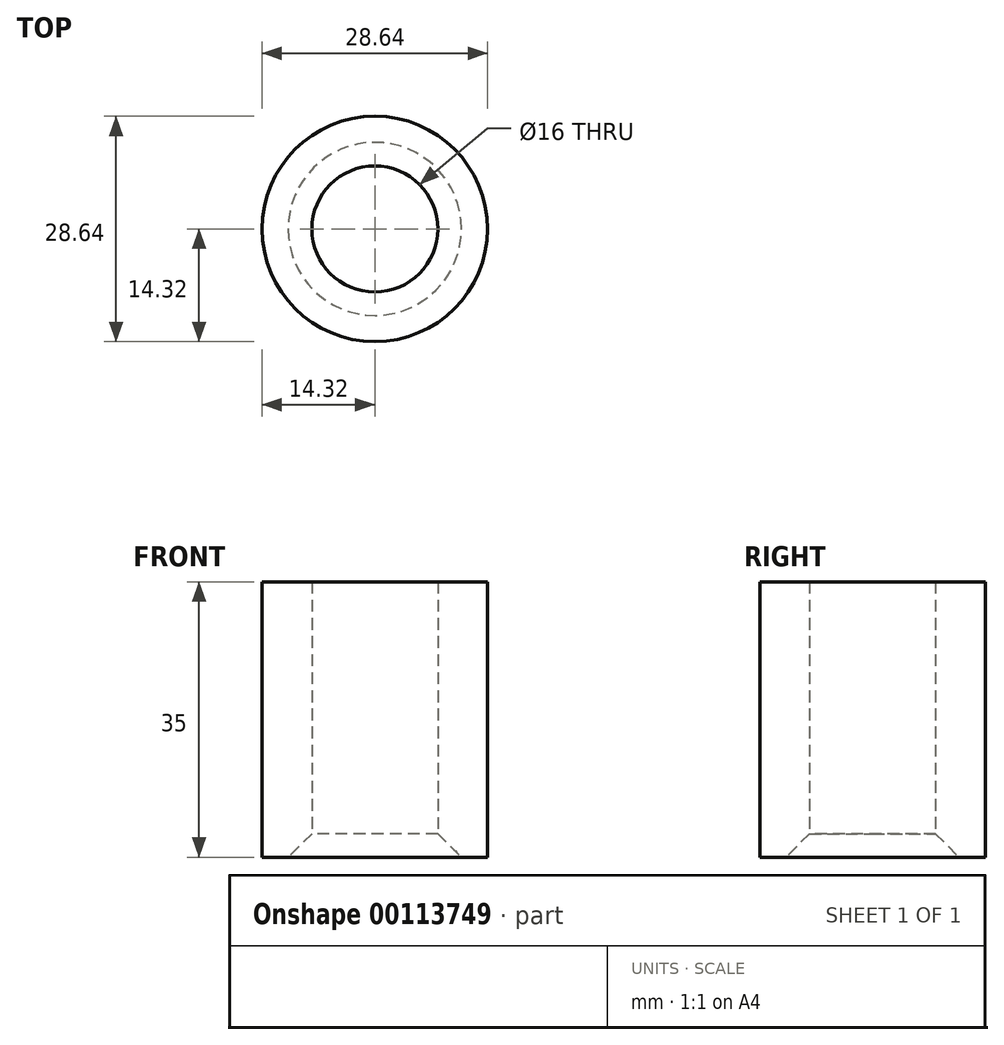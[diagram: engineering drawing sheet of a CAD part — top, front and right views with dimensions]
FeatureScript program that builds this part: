
annotation { "Feature Type Name" : "Feature", "Feature Type Description" : "" }
export const myFeature = defineFeature(function(context is Context, id is Id, definition is map)
    precondition{}
    {
        {
            var Q0;
            Q0=qCreatedBy(makeId("Top.planeOp"),FACE);
            var sketch = newSketch(context, id + "F0", { "sketchPlane" : qUnion([Q0])});
            skCircle(sketch, "E0", {"center": v(0, 0) * mm, "radius": 8 * mm});
            skCircle(sketch, "E1", {"center": v(0, 0) * mm, "radius": 14.31 * mm});
            skSolve(sketch);
        }
        {
            var Q0;
            Q0=makeQuery(id+"F0.imprint","IMPRINT",FACE,{"disambiguationData":[TD([[makeQuery(id+"F0.imprint","IMPRINT",EDGE,{"derivedFrom":sQuery(id+"F0.wireOp",EDGE,"E0")}),-1.0]])]});
            extrude(context, id + "F1", {"entities" : qUnion([Q0]), "depth" : 35 * mm});
        }
        {
            var Q0;
            Q0=makeQuery(id+"F1.opExtrude","CAP_EDGE",EDGE,{"disambiguationData":[OSD([sQuery(id+"F0.wireOp",EDGE,"E0")])],"isStart":true});
            chamfer(context, id + "F2", {"entities" : qUnion([Q0]), "width" : 3 * mm, "tangentPropagation" : true});
        }
    });
